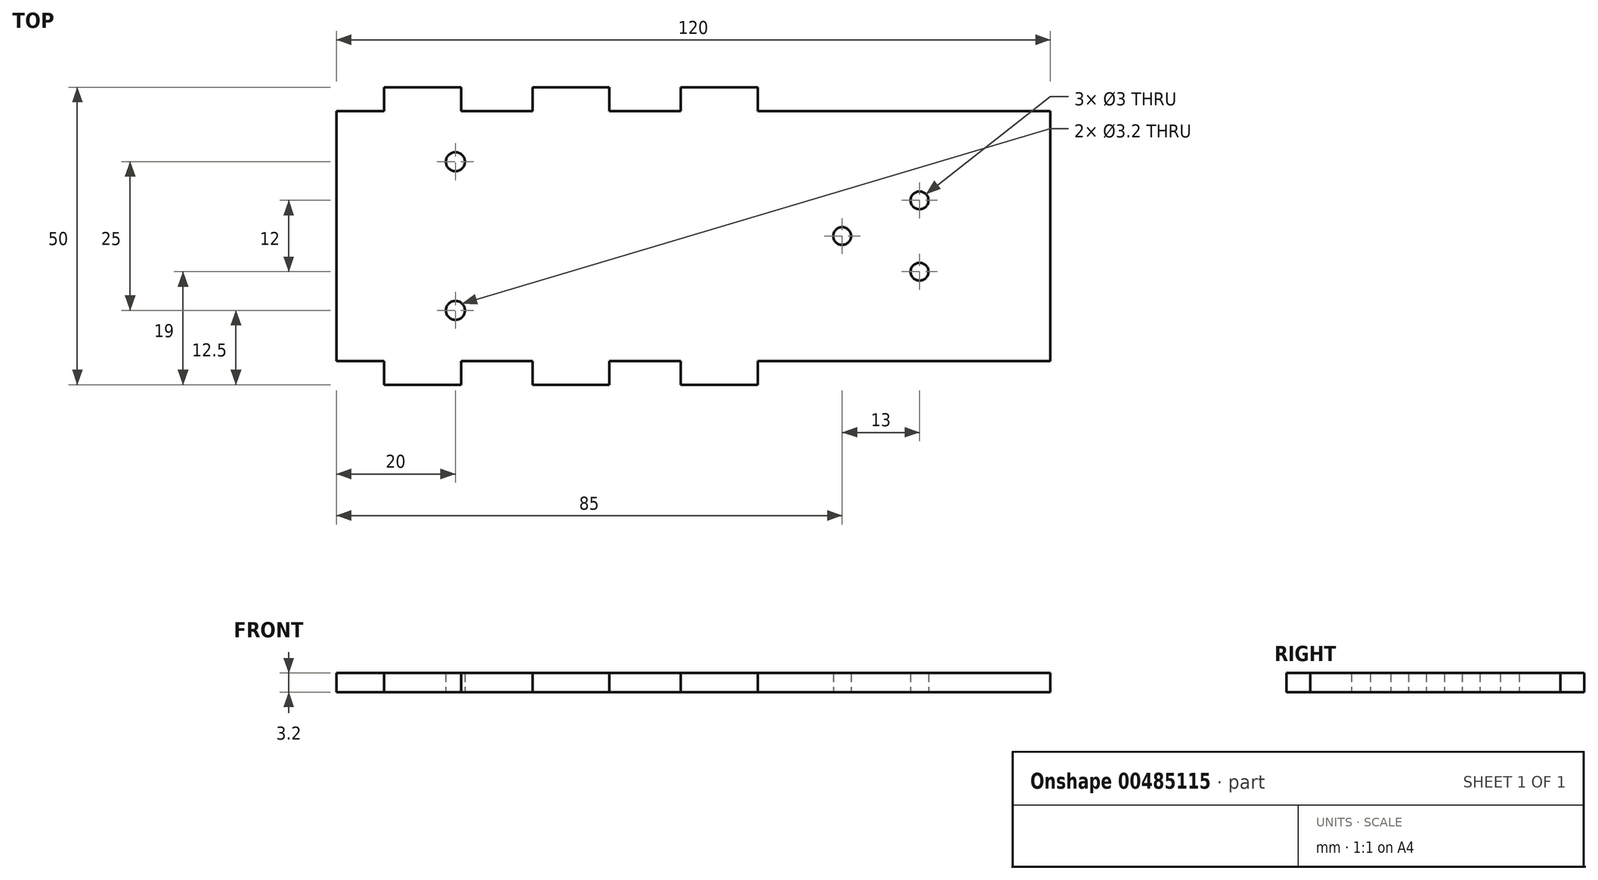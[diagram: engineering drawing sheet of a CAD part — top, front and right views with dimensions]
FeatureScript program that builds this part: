
annotation { "Feature Type Name" : "Feature", "Feature Type Description" : "" }
export const myFeature = defineFeature(function(context is Context, id is Id, definition is map)
    precondition{}
    {
        {
            var Q0;
            Q0=qCreatedBy(makeId("Top.planeOp"),FACE);
            var sketch = newSketch(context, id + "F0", { "sketchPlane" : qUnion([Q0])});
            skLineSegment(sketch, "E0.bottom", {"start": v(-60, 25) * mm, "end": v(60, 25) * mm, "construction": true});
            skLineSegment(sketch, "E0.top", {"start": v(-60, -25) * mm, "end": v(60, -25) * mm, "construction": true});
            skLineSegment(sketch, "E0.left", {"start": v(-60, 25) * mm, "end": v(-60, -25) * mm, "construction": true});
            skLineSegment(sketch, "E0.right", {"start": v(60, 25) * mm, "end": v(60, -25) * mm, "construction": true});
            skPoint(sketch, "E0.middle", {"position": v(0, 0) * mm});
            skLineSegment(sketch, "E1", {"start": v(-60, 21) * mm, "end": v(60, 21) * mm, "construction": true});
            skLineSegment(sketch, "E2", {"start": v(-60, -21) * mm, "end": v(60, -21) * mm, "construction": true});
            skLineSegment(sketch, "E3", {"start": v(-52, 25) * mm, "end": v(-52, -25) * mm, "construction": true});
            skLineSegment(sketch, "E4", {"start": v(-39.05, 25) * mm, "end": v(-39.05, -25) * mm, "construction": true});
            skLineSegment(sketch, "E5", {"start": v(-27.05, 25) * mm, "end": v(-27.05, -25) * mm, "construction": true});
            skLineSegment(sketch, "E6", {"start": v(-14.1, 25) * mm, "end": v(-14.1, -25) * mm, "construction": true});
            skLineSegment(sketch, "E7", {"start": v(-2.1, 25) * mm, "end": v(-2.1, -25) * mm, "construction": true});
            skLineSegment(sketch, "E8", {"start": v(10.85, 25) * mm, "end": v(10.85, -25) * mm, "construction": true});
            skLineSegment(sketch, "E9", {"start": v(-60, 21) * mm, "end": v(-52, 21) * mm});
            skLineSegment(sketch, "E10", {"start": v(-52, 21) * mm, "end": v(-52, 25) * mm});
            skLineSegment(sketch, "E11", {"start": v(-39.05, 25) * mm, "end": v(-52, 25) * mm});
            skLineSegment(sketch, "E12", {"start": v(-27.05, 25) * mm, "end": v(-14.1, 25) * mm});
            skLineSegment(sketch, "E13", {"start": v(-2.1, 25) * mm, "end": v(10.85, 25) * mm});
            skLineSegment(sketch, "E14", {"start": v(10.85, 25) * mm, "end": v(10.85, 21) * mm});
            skLineSegment(sketch, "E15", {"start": v(10.85, 21) * mm, "end": v(60, 21) * mm});
            skLineSegment(sketch, "E16", {"start": v(-60, 21) * mm, "end": v(-60, -21) * mm});
            skLineSegment(sketch, "E17", {"start": v(-60, -21) * mm, "end": v(-52, -21) * mm});
            skLineSegment(sketch, "E18", {"start": v(-52, -21) * mm, "end": v(-52, -25) * mm});
            skLineSegment(sketch, "E19", {"start": v(-52, -25) * mm, "end": v(-39.05, -25) * mm});
            skLineSegment(sketch, "E20", {"start": v(-27.05, -25) * mm, "end": v(-14.1, -25) * mm});
            skLineSegment(sketch, "E21", {"start": v(-2.1, -25) * mm, "end": v(10.85, -25) * mm});
            skLineSegment(sketch, "E22", {"start": v(-39.05, -25) * mm, "end": v(-39.05, -21) * mm});
            skLineSegment(sketch, "E23", {"start": v(-39.05, -21) * mm, "end": v(-27.05, -21) * mm});
            skLineSegment(sketch, "E24", {"start": v(-27.05, -21) * mm, "end": v(-27.05, -25) * mm});
            skLineSegment(sketch, "E25", {"start": v(-14.1, -25) * mm, "end": v(-14.1, -21) * mm});
            skLineSegment(sketch, "E26", {"start": v(-14.1, -21) * mm, "end": v(-2.1, -21) * mm});
            skLineSegment(sketch, "E27", {"start": v(-2.1, -21) * mm, "end": v(-2.1, -25) * mm});
            skLineSegment(sketch, "E28", {"start": v(10.85, -25) * mm, "end": v(10.85, -21) * mm});
            skLineSegment(sketch, "E29", {"start": v(10.85, -21) * mm, "end": v(60, -21) * mm});
            skLineSegment(sketch, "E30", {"start": v(60, 21) * mm, "end": v(60, -21) * mm});
            skLineSegment(sketch, "E31", {"start": v(-2.1, 25) * mm, "end": v(-2.1, 21) * mm});
            skLineSegment(sketch, "E32", {"start": v(-2.1, 21) * mm, "end": v(-14.1, 21) * mm});
            skLineSegment(sketch, "E33", {"start": v(-14.1, 21) * mm, "end": v(-14.1, 25) * mm});
            skLineSegment(sketch, "E34", {"start": v(-27.05, 25) * mm, "end": v(-27.05, 21) * mm});
            skLineSegment(sketch, "E35", {"start": v(-27.05, 21) * mm, "end": v(-39.05, 21) * mm});
            skLineSegment(sketch, "E36", {"start": v(-39.05, 21) * mm, "end": v(-39.05, 25) * mm});
            skLineSegment(sketch, "E37", {"start": v(-60, 0) * mm, "end": v(60, 0) * mm, "construction": true});
            skLineSegment(sketch, "E38", {"start": v(-60, 12.5) * mm, "end": v(60, 12.5) * mm, "construction": true});
            skLineSegment(sketch, "E39", {"start": v(-60, -12.5) * mm, "end": v(60, -12.5) * mm, "construction": true});
            skPoint(sketch, "E40", {"position": v(-40, 12.5) * mm});
            skPoint(sketch, "E41", {"position": v(-40, -12.5) * mm});
            skCircle(sketch, "E42", {"center": v(-40, 12.5) * mm, "radius": 1.6 * mm});
            skCircle(sketch, "E43", {"center": v(-40, -12.5) * mm, "radius": 1.6 * mm});
            skLineSegment(sketch, "E44", {"start": v(-40, 12.5) * mm, "end": v(-40, -12.5) * mm, "construction": true});
            skLineSegment(sketch, "E45", {"start": v(60, 6) * mm, "end": v(10.85, 6) * mm, "construction": true});
            skLineSegment(sketch, "E46", {"start": v(60, -6) * mm, "end": v(10.85, -6) * mm, "construction": true});
            skLineSegment(sketch, "E47", {"start": v(38, 6) * mm, "end": v(38, -6) * mm, "construction": true});
            skLineSegment(sketch, "E48", {"start": v(25, 6) * mm, "end": v(25, -6) * mm, "construction": true});
            skCircle(sketch, "E49", {"center": v(25, 0) * mm, "radius": 1.5 * mm});
            skCircle(sketch, "E50", {"center": v(38, 6) * mm, "radius": 1.5 * mm});
            skCircle(sketch, "E51", {"center": v(38, -6) * mm, "radius": 1.5 * mm});
            skSolve(sketch);
        }
        {
            var Q0;
            Q0=makeQuery(id+"F0.imprint","IMPRINT",FACE,{"disambiguationData":[TD([[makeQuery(id+"F0.imprint","IMPRINT",EDGE,{"derivedFrom":sQuery(id+"F0.wireOp",EDGE,"E9")}),-1.0]])]});
            extrude(context, id + "F1", {"entities" : qUnion([Q0]), "depth" : 3.2 * mm, "offsetDistance" : 25 * mm});
        }
    });
